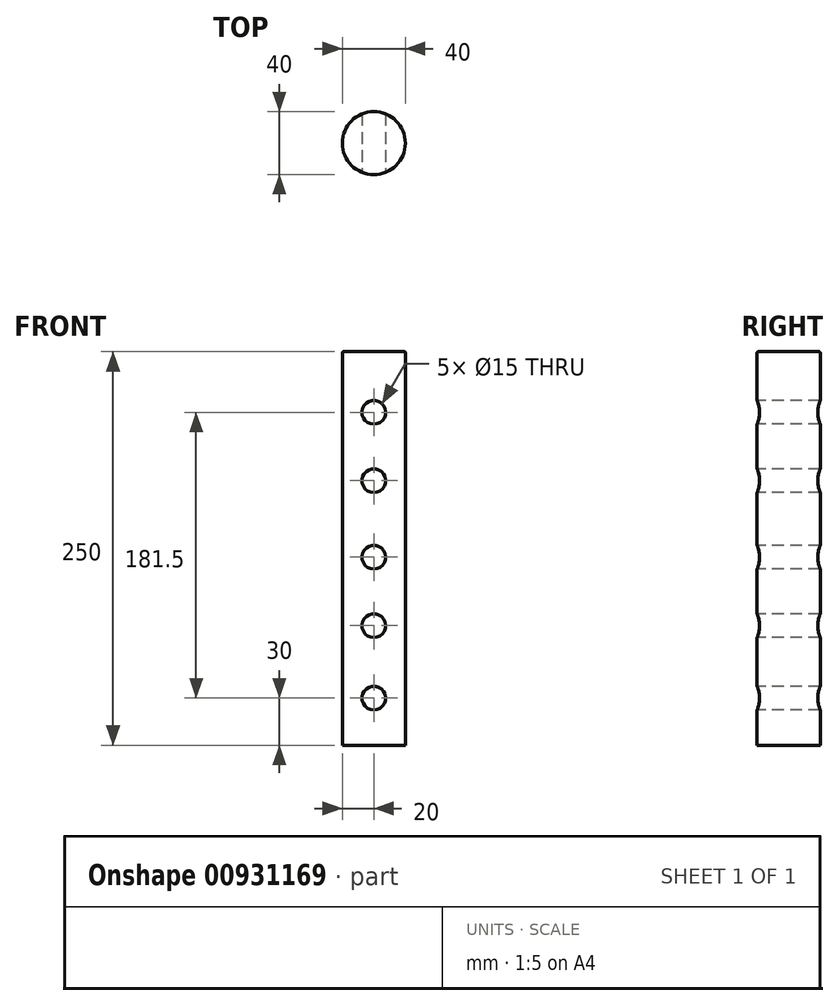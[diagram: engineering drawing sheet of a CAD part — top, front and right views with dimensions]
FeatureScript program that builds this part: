
annotation { "Feature Type Name" : "Feature", "Feature Type Description" : "" }
export const myFeature = defineFeature(function(context is Context, id is Id, definition is map)
    precondition{}
    {
        {
            var Q0;
            Q0=qCreatedBy(makeId("Top.planeOp"),FACE);
            var sketch = newSketch(context, id + "F0", { "sketchPlane" : qUnion([Q0])});
            skCircle(sketch, "E0", {"center": v(0, 20) * mm, "radius": 20 * mm});
            skSolve(sketch);
        }
        {
            var Q0;
            Q0=makeQuery(id+"F0.imprint","IMPRINT",FACE,{"disambiguationData":[TD([[makeQuery(id+"F0.imprint","IMPRINT",EDGE,{"derivedFrom":sQuery(id+"F0.wireOp",EDGE,"OIBgse5x-OCEe-grOV-zcti-46tkXojFW9II")}),1.0]])]});
            var Q1;
            Q1=makeQuery(id+"F0.imprint","IMPRINT",FACE,{"disambiguationData":[TD([[makeQuery(id+"F0.imprint","IMPRINT",EDGE,{"derivedFrom":sQuery(id+"F0.wireOp",EDGE,"E0")}),1.0]])]});
            extrude(context, id + "F1", {"entities" : qUnion([Q0, Q1]), "depth" : 250 * mm, "offsetDistance" : 25 * mm});
        }
        {
            var Q0;
            Q0=qCreatedBy(makeId("Front.planeOp"),FACE);
            var sketch = newSketch(context, id + "F2", { "sketchPlane" : qUnion([Q0])});
            skLineSegment(sketch, "E1", {"start": v(0, 0) * mm, "end": v(0, 239) * mm, "construction": true});
            skPoint(sketch, "E2", {"position": v(0, 30) * mm});
            skPoint(sketch, "E3", {"position": v(0, 76) * mm});
            skPoint(sketch, "E4", {"position": v(0, 119.5) * mm});
            skPoint(sketch, "E5", {"position": v(0, 168.1) * mm});
            skPoint(sketch, "E6", {"position": v(0, 211.5) * mm});
            skSolve(sketch);
        }
        {
            var Q0;
            Q0=sQuery(id+"F2.wireOp",VERTEX,"E2");
            var Q1;
            Q1=sQuery(id+"F2.wireOp",VERTEX,"E3");
            var Q2;
            Q2=sQuery(id+"F2.wireOp",VERTEX,"E4");
            var Q3;
            Q3=sQuery(id+"F2.wireOp",VERTEX,"E5");
            var Q4;
            Q4=sQuery(id+"F2.wireOp",VERTEX,"E6");
            var Q5;
            Q5=makeQuery(id+"F1.opExtrude","SWEPT_BODY",BODY,{"disambiguationData":[OSD([sQuery(id+"F0.wireOp",EDGE,"OIBgse5x-OCEe-grOV-zcti-46tkXojFW9II")])]});
            var Q6;
            Q6=makeQuery(id+"F1.opExtrude","SWEPT_BODY",BODY,{"disambiguationData":[OSD([sQuery(id+"F0.wireOp",EDGE,"E0")])]});
            hole(context, id + "F3", {"style" : HoleStyle.SIMPLE, "endStyle" : HoleEndStyle.THROUGH, "standardTappedOrClearance" : lookupTablePath({ "standard" : "ISO", "size" : "15", "type" : "Drilled" }), "standardBlindInLast" : lookupTablePath({ "standard" : "ISO", "size" : "15", "type" : "Drilled" }), "holeDiameter" : 15 * mm, "majorDiameter" : 10 * mm, "isTappedThrough" : true, "tappedDepth" : 12 * mm, "tapClearance" : 3, "startFromSketch" : true, "locations" : qUnion([Q0, Q1, Q2, Q3, Q4]), "scope" : qUnion([Q5, Q6])});
        }
        {
            var Q0;
            Q0=makeQuery(id+"F3.hole-1.boolean.opBoolean","INTERSECT",EDGE,{"disambiguationData":[OD(0.0)],"derivedFrom":[makeQuery(id+"F1.opExtrude","SWEPT_FACE",FACE,{"disambiguationData":[OSD([sQuery(id+"F0.wireOp",EDGE,"E0")])]}),makeQuery(id+"F3.hole-1.opRevolve","SWEPT_FACE",FACE,{"disambiguationData":[OSD([sQuery(id+"F3.hole-1.sketch.wireOp",EDGE,"core_line_2")])]})]});
            var Q1;
            Q1=makeQuery(id+"F3.hole-0.boolean.opBoolean","INTERSECT",EDGE,{"disambiguationData":[OD(0.0)],"derivedFrom":[makeQuery(id+"F1.opExtrude","SWEPT_FACE",FACE,{"disambiguationData":[OSD([sQuery(id+"F0.wireOp",EDGE,"E0")])]}),makeQuery(id+"F3.hole-0.opRevolve","SWEPT_FACE",FACE,{"disambiguationData":[OSD([sQuery(id+"F3.hole-0.sketch.wireOp",EDGE,"core_line_2")])]})]});
            var Q2;
            Q2=makeQuery(id+"F3.hole-2.boolean.opBoolean","INTERSECT",EDGE,{"disambiguationData":[OD(0.0)],"derivedFrom":[makeQuery(id+"F1.opExtrude","SWEPT_FACE",FACE,{"disambiguationData":[OSD([sQuery(id+"F0.wireOp",EDGE,"E0")])]}),makeQuery(id+"F3.hole-2.opRevolve","SWEPT_FACE",FACE,{"disambiguationData":[OSD([sQuery(id+"F3.hole-2.sketch.wireOp",EDGE,"core_line_2")])]})]});
            var Q3;
            Q3=makeQuery(id+"F3.hole-3.boolean.opBoolean","INTERSECT",EDGE,{"disambiguationData":[OD(0.0)],"derivedFrom":[makeQuery(id+"F1.opExtrude","SWEPT_FACE",FACE,{"disambiguationData":[OSD([sQuery(id+"F0.wireOp",EDGE,"E0")])]}),makeQuery(id+"F3.hole-3.opRevolve","SWEPT_FACE",FACE,{"disambiguationData":[OSD([sQuery(id+"F3.hole-3.sketch.wireOp",EDGE,"core_line_2")])]})]});
            var Q4;
            Q4=makeQuery(id+"F3.hole-4.boolean.opBoolean","INTERSECT",EDGE,{"disambiguationData":[OD(0.0)],"derivedFrom":[makeQuery(id+"F1.opExtrude","SWEPT_FACE",FACE,{"disambiguationData":[OSD([sQuery(id+"F0.wireOp",EDGE,"E0")])]}),makeQuery(id+"F3.hole-4.opRevolve","SWEPT_FACE",FACE,{"disambiguationData":[OSD([sQuery(id+"F3.hole-4.sketch.wireOp",EDGE,"core_line_2")])]})]});
            var Q5;
            Q5=makeQuery(id+"F1.opExtrude","CAP_EDGE",EDGE,{"disambiguationData":[OSD([sQuery(id+"F0.wireOp",EDGE,"E0")])],"isStart":false});
            var Q6;
            Q6=makeQuery(id+"F3.hole-4.boolean.opBoolean","INTERSECT",EDGE,{"disambiguationData":[OD(1.0)],"derivedFrom":[makeQuery(id+"F1.opExtrude","SWEPT_FACE",FACE,{"disambiguationData":[OSD([sQuery(id+"F0.wireOp",EDGE,"E0")])]}),makeQuery(id+"F3.hole-4.opRevolve","SWEPT_FACE",FACE,{"disambiguationData":[OSD([sQuery(id+"F3.hole-4.sketch.wireOp",EDGE,"core_line_2")])]})]});
            var Q7;
            Q7=makeQuery(id+"F3.hole-3.boolean.opBoolean","INTERSECT",EDGE,{"disambiguationData":[OD(1.0)],"derivedFrom":[makeQuery(id+"F1.opExtrude","SWEPT_FACE",FACE,{"disambiguationData":[OSD([sQuery(id+"F0.wireOp",EDGE,"E0")])]}),makeQuery(id+"F3.hole-3.opRevolve","SWEPT_FACE",FACE,{"disambiguationData":[OSD([sQuery(id+"F3.hole-3.sketch.wireOp",EDGE,"core_line_2")])]})]});
            var Q8;
            Q8=makeQuery(id+"F3.hole-2.boolean.opBoolean","INTERSECT",EDGE,{"disambiguationData":[OD(1.0)],"derivedFrom":[makeQuery(id+"F1.opExtrude","SWEPT_FACE",FACE,{"disambiguationData":[OSD([sQuery(id+"F0.wireOp",EDGE,"E0")])]}),makeQuery(id+"F3.hole-2.opRevolve","SWEPT_FACE",FACE,{"disambiguationData":[OSD([sQuery(id+"F3.hole-2.sketch.wireOp",EDGE,"core_line_2")])]})]});
            var Q9;
            Q9=makeQuery(id+"F3.hole-1.boolean.opBoolean","INTERSECT",EDGE,{"disambiguationData":[OD(1.0)],"derivedFrom":[makeQuery(id+"F1.opExtrude","SWEPT_FACE",FACE,{"disambiguationData":[OSD([sQuery(id+"F0.wireOp",EDGE,"E0")])]}),makeQuery(id+"F3.hole-1.opRevolve","SWEPT_FACE",FACE,{"disambiguationData":[OSD([sQuery(id+"F3.hole-1.sketch.wireOp",EDGE,"core_line_2")])]})]});
            var Q10;
            Q10=makeQuery(id+"F3.hole-0.boolean.opBoolean","INTERSECT",EDGE,{"disambiguationData":[OD(1.0)],"derivedFrom":[makeQuery(id+"F1.opExtrude","SWEPT_FACE",FACE,{"disambiguationData":[OSD([sQuery(id+"F0.wireOp",EDGE,"E0")])]}),makeQuery(id+"F3.hole-0.opRevolve","SWEPT_FACE",FACE,{"disambiguationData":[OSD([sQuery(id+"F3.hole-0.sketch.wireOp",EDGE,"core_line_2")])]})]});
            fillet(context, id + "F4", {"entities" : qUnion([Q0, Q1, Q2, Q3, Q4, Q5, Q6, Q7, Q8, Q9, Q10]), "radius" : 0.5 * mm, "tangentPropagation" : true, "allowEdgeOverflow" : false});
        }
    });
